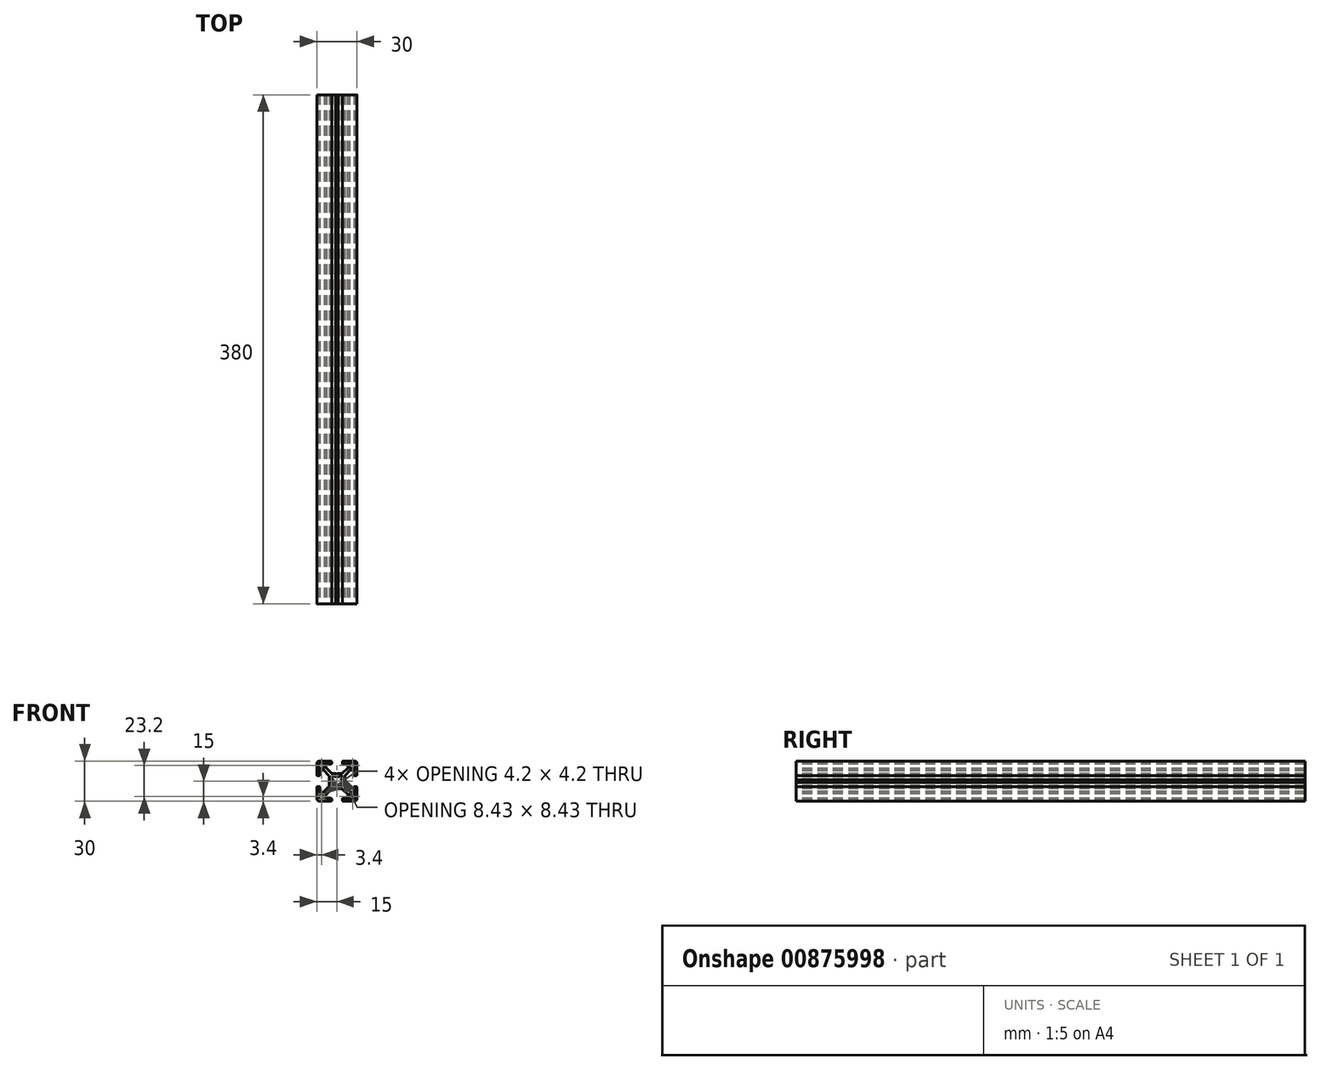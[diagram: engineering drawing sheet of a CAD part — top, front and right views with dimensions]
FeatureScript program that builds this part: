
annotation { "Feature Type Name" : "Feature", "Feature Type Description" : "" }
export const myFeature = defineFeature(function(context is Context, id is Id, definition is map)
    precondition{}
    {
        {
            var Q0;
            Q0=qCreatedBy(makeId("Front.planeOp"),FACE);
            var sketch = newSketch(context, id + "F0", { "sketchPlane" : qUnion([Q0])});
            skArc(sketch, "E0", {"start": v(9.88, 13.7) * mm, "mid": v(9.61, 13.59) * mm, "end": v(9.5, 13.32) * mm});
            skLineSegment(sketch, "E1", {"start": v(12.7, 13.7) * mm, "end": v(9.88, 13.7) * mm});
            skArc(sketch, "E2", {"start": v(13.7, 12.7) * mm, "mid": v(13.4, 13.4) * mm, "end": v(12.7, 13.7) * mm});
            skLineSegment(sketch, "E3", {"start": v(13.7, 9.88) * mm, "end": v(13.7, 12.7) * mm});
            skArc(sketch, "E4", {"start": v(13.32, 9.5) * mm, "mid": v(13.59, 9.61) * mm, "end": v(13.7, 9.88) * mm});
            skLineSegment(sketch, "E5", {"start": v(9.88, 9.5) * mm, "end": v(13.32, 9.5) * mm});
            skArc(sketch, "E6", {"start": v(9.5, 9.88) * mm, "mid": v(9.61, 9.61) * mm, "end": v(9.88, 9.5) * mm});
            skLineSegment(sketch, "E7", {"start": v(9.5, 13.32) * mm, "end": v(9.5, 9.88) * mm});
            skArc(sketch, "E8", {"start": v(-9.5, 13.32) * mm, "mid": v(-9.61, 13.59) * mm, "end": v(-9.88, 13.7) * mm});
            skLineSegment(sketch, "E9", {"start": v(-9.5, 9.88) * mm, "end": v(-9.5, 13.32) * mm});
            skArc(sketch, "E10", {"start": v(-9.88, 9.5) * mm, "mid": v(-9.61, 9.61) * mm, "end": v(-9.5, 9.88) * mm});
            skLineSegment(sketch, "E11", {"start": v(-13.32, 9.5) * mm, "end": v(-9.88, 9.5) * mm});
            skArc(sketch, "E12", {"start": v(-13.7, 9.88) * mm, "mid": v(-13.59, 9.61) * mm, "end": v(-13.32, 9.5) * mm});
            skLineSegment(sketch, "E13", {"start": v(-13.7, 12.7) * mm, "end": v(-13.7, 9.88) * mm});
            skArc(sketch, "E14", {"start": v(-12.7, 13.7) * mm, "mid": v(-13.4, 13.4) * mm, "end": v(-13.7, 12.7) * mm});
            skLineSegment(sketch, "E15", {"start": v(-9.88, 13.7) * mm, "end": v(-12.7, 13.7) * mm});
            skArc(sketch, "E16", {"start": v(-1.5, -3.2) * mm, "mid": v(0, -3.53) * mm, "end": v(1.5, -3.2) * mm});
            skLineSegment(sketch, "E17", {"start": v(-2.47, -3.98) * mm, "end": v(-1.5, -3.2) * mm});
            skArc(sketch, "E18", {"start": v(-3.98, -2.47) * mm, "mid": v(-3.9, -3.9) * mm, "end": v(-2.47, -3.98) * mm});
            skLineSegment(sketch, "E19", {"start": v(-3.2, -1.5) * mm, "end": v(-3.98, -2.47) * mm});
            skArc(sketch, "E20", {"start": v(-3.2, 1.5) * mm, "mid": v(-3.53, 0) * mm, "end": v(-3.2, -1.5) * mm});
            skLineSegment(sketch, "E21", {"start": v(-3.98, 2.47) * mm, "end": v(-3.2, 1.5) * mm});
            skArc(sketch, "E22", {"start": v(-2.47, 3.98) * mm, "mid": v(-3.9, 3.9) * mm, "end": v(-3.98, 2.47) * mm});
            skLineSegment(sketch, "E23", {"start": v(-1.5, 3.2) * mm, "end": v(-2.47, 3.98) * mm});
            skArc(sketch, "E24", {"start": v(1.5, 3.2) * mm, "mid": v(0, 3.53) * mm, "end": v(-1.5, 3.2) * mm});
            skLineSegment(sketch, "E25", {"start": v(2.47, 3.98) * mm, "end": v(1.5, 3.2) * mm});
            skArc(sketch, "E26", {"start": v(3.98, 2.47) * mm, "mid": v(3.9, 3.9) * mm, "end": v(2.47, 3.98) * mm});
            skLineSegment(sketch, "E27", {"start": v(3.2, 1.5) * mm, "end": v(3.98, 2.47) * mm});
            skArc(sketch, "E28", {"start": v(3.2, -1.5) * mm, "mid": v(3.53, 0) * mm, "end": v(3.2, 1.5) * mm});
            skLineSegment(sketch, "E29", {"start": v(3.98, -2.47) * mm, "end": v(3.2, -1.5) * mm});
            skArc(sketch, "E30", {"start": v(2.47, -3.98) * mm, "mid": v(3.9, -3.9) * mm, "end": v(3.98, -2.47) * mm});
            skLineSegment(sketch, "E31", {"start": v(1.5, -3.2) * mm, "end": v(2.47, -3.98) * mm});
            skArc(sketch, "E32", {"start": v(-13.32, -9.5) * mm, "mid": v(-13.59, -9.61) * mm, "end": v(-13.7, -9.88) * mm});
            skLineSegment(sketch, "E33", {"start": v(-9.88, -9.5) * mm, "end": v(-13.32, -9.5) * mm});
            skArc(sketch, "E34", {"start": v(-9.5, -9.88) * mm, "mid": v(-9.61, -9.61) * mm, "end": v(-9.88, -9.5) * mm});
            skLineSegment(sketch, "E35", {"start": v(-9.5, -13.32) * mm, "end": v(-9.5, -9.88) * mm});
            skArc(sketch, "E36", {"start": v(-9.88, -13.7) * mm, "mid": v(-9.61, -13.59) * mm, "end": v(-9.5, -13.32) * mm});
            skLineSegment(sketch, "E37", {"start": v(-12.7, -13.7) * mm, "end": v(-9.88, -13.7) * mm});
            skArc(sketch, "E38", {"start": v(-13.7, -12.7) * mm, "mid": v(-13.4, -13.4) * mm, "end": v(-12.7, -13.7) * mm});
            skLineSegment(sketch, "E39", {"start": v(-13.7, -9.88) * mm, "end": v(-13.7, -12.7) * mm});
            skArc(sketch, "E40", {"start": v(9.5, -13.32) * mm, "mid": v(9.61, -13.59) * mm, "end": v(9.88, -13.7) * mm});
            skLineSegment(sketch, "E41", {"start": v(9.5, -9.88) * mm, "end": v(9.5, -13.32) * mm});
            skArc(sketch, "E42", {"start": v(9.88, -9.5) * mm, "mid": v(9.61, -9.61) * mm, "end": v(9.5, -9.88) * mm});
            skLineSegment(sketch, "E43", {"start": v(13.32, -9.5) * mm, "end": v(9.88, -9.5) * mm});
            skArc(sketch, "E44", {"start": v(13.7, -9.88) * mm, "mid": v(13.59, -9.61) * mm, "end": v(13.32, -9.5) * mm});
            skLineSegment(sketch, "E45", {"start": v(13.7, -12.7) * mm, "end": v(13.7, -9.88) * mm});
            skArc(sketch, "E46", {"start": v(12.7, -13.7) * mm, "mid": v(13.4, -13.4) * mm, "end": v(13.7, -12.7) * mm});
            skLineSegment(sketch, "E47", {"start": v(9.88, -13.7) * mm, "end": v(12.7, -13.7) * mm});
            skArc(sketch, "E48", {"start": v(13.24, -4) * mm, "mid": v(12.89, -4.15) * mm, "end": v(12.74, -4.5) * mm});
            skLineSegment(sketch, "E49", {"start": v(12.74, -4.5) * mm, "end": v(12.74, -7.73) * mm});
            skArc(sketch, "E50", {"start": v(12.24, -8.25) * mm, "mid": v(12.6, -8.1) * mm, "end": v(12.74, -7.73) * mm});
            skLineSegment(sketch, "E51", {"start": v(12.24, -8.25) * mm, "end": v(10.26, -8.25) * mm});
            skArc(sketch, "E52", {"start": v(9.9, -8.1) * mm, "mid": v(10.07, -8.21) * mm, "end": v(10.26, -8.25) * mm});
            skLineSegment(sketch, "E53", {"start": v(9.9, -8.1) * mm, "end": v(5.98, -4.18) * mm});
            skArc(sketch, "E54", {"start": v(5.83, -3.82) * mm, "mid": v(5.87, -4.02) * mm, "end": v(5.98, -4.18) * mm});
            skLineSegment(sketch, "E55", {"start": v(5.83, -3.82) * mm, "end": v(5.83, -1.01) * mm});
            skLineSegment(sketch, "E56", {"start": v(5.83, -1.01) * mm, "end": v(5.32, -0.06) * mm});
            skLineSegment(sketch, "E57", {"start": v(5.32, -0.06) * mm, "end": v(5.83, 0.89) * mm});
            skLineSegment(sketch, "E58", {"start": v(5.83, 0.89) * mm, "end": v(5.83, 3.82) * mm});
            skArc(sketch, "E59", {"start": v(5.98, 4.18) * mm, "mid": v(5.87, 4.02) * mm, "end": v(5.83, 3.82) * mm});
            skLineSegment(sketch, "E60", {"start": v(5.98, 4.18) * mm, "end": v(9.9, 8.1) * mm});
            skArc(sketch, "E61", {"start": v(10.26, 8.25) * mm, "mid": v(10.07, 8.21) * mm, "end": v(9.9, 8.1) * mm});
            skLineSegment(sketch, "E62", {"start": v(10.26, 8.25) * mm, "end": v(12.24, 8.25) * mm});
            skArc(sketch, "E63", {"start": v(12.74, 7.73) * mm, "mid": v(12.6, 8.1) * mm, "end": v(12.24, 8.25) * mm});
            skLineSegment(sketch, "E64", {"start": v(12.74, 7.73) * mm, "end": v(12.74, 4.5) * mm});
            skArc(sketch, "E65", {"start": v(12.74, 4.5) * mm, "mid": v(12.89, 4.15) * mm, "end": v(13.24, 4) * mm});
            skLineSegment(sketch, "E66", {"start": v(13.24, 4) * mm, "end": v(14.5, 4) * mm});
            skArc(sketch, "E67", {"start": v(14.5, 4) * mm, "mid": v(14.85, 4.15) * mm, "end": v(15, 4.5) * mm});
            skLineSegment(sketch, "E68", {"start": v(15, 4.5) * mm, "end": v(15, 13) * mm});
            skArc(sketch, "E69", {"start": v(15, 13) * mm, "mid": v(14.41, 14.41) * mm, "end": v(13, 15) * mm});
            skLineSegment(sketch, "E70", {"start": v(13, 15) * mm, "end": v(4.5, 15) * mm});
            skArc(sketch, "E71", {"start": v(4.5, 15) * mm, "mid": v(4.15, 14.85) * mm, "end": v(4, 14.5) * mm});
            skLineSegment(sketch, "E72", {"start": v(4, 14.5) * mm, "end": v(4, 13.24) * mm});
            skArc(sketch, "E73", {"start": v(4, 13.24) * mm, "mid": v(4.15, 12.89) * mm, "end": v(4.5, 12.74) * mm});
            skLineSegment(sketch, "E74", {"start": v(4.5, 12.74) * mm, "end": v(7.73, 12.74) * mm});
            skArc(sketch, "E75", {"start": v(8.25, 12.24) * mm, "mid": v(8.1, 12.6) * mm, "end": v(7.73, 12.74) * mm});
            skLineSegment(sketch, "E76", {"start": v(8.25, 12.24) * mm, "end": v(8.25, 10.26) * mm});
            skArc(sketch, "E77", {"start": v(8.1, 9.9) * mm, "mid": v(8.21, 10.07) * mm, "end": v(8.25, 10.26) * mm});
            skLineSegment(sketch, "E78", {"start": v(8.1, 9.9) * mm, "end": v(4.18, 5.98) * mm});
            skArc(sketch, "E79", {"start": v(3.82, 5.83) * mm, "mid": v(4.02, 5.87) * mm, "end": v(4.18, 5.98) * mm});
            skLineSegment(sketch, "E80", {"start": v(3.82, 5.83) * mm, "end": v(0.95, 5.83) * mm});
            skLineSegment(sketch, "E81", {"start": v(0.95, 5.83) * mm, "end": v(0, 5.32) * mm});
            skLineSegment(sketch, "E82", {"start": v(0, 5.32) * mm, "end": v(-0.95, 5.83) * mm});
            skLineSegment(sketch, "E83", {"start": v(-0.95, 5.83) * mm, "end": v(-3.82, 5.83) * mm});
            skArc(sketch, "E84", {"start": v(-4.18, 5.98) * mm, "mid": v(-4.02, 5.87) * mm, "end": v(-3.82, 5.83) * mm});
            skLineSegment(sketch, "E85", {"start": v(-4.18, 5.98) * mm, "end": v(-8.1, 9.9) * mm});
            skArc(sketch, "E86", {"start": v(-8.25, 10.26) * mm, "mid": v(-8.21, 10.07) * mm, "end": v(-8.1, 9.9) * mm});
            skLineSegment(sketch, "E87", {"start": v(-8.25, 10.26) * mm, "end": v(-8.25, 12.24) * mm});
            skArc(sketch, "E88", {"start": v(-7.73, 12.74) * mm, "mid": v(-8.1, 12.6) * mm, "end": v(-8.25, 12.24) * mm});
            skLineSegment(sketch, "E89", {"start": v(-7.73, 12.74) * mm, "end": v(-4.5, 12.74) * mm});
            skArc(sketch, "E90", {"start": v(-4.5, 12.74) * mm, "mid": v(-4.15, 12.89) * mm, "end": v(-4, 13.24) * mm});
            skLineSegment(sketch, "E91", {"start": v(-4, 13.24) * mm, "end": v(-4, 14.5) * mm});
            skArc(sketch, "E92", {"start": v(-4, 14.5) * mm, "mid": v(-4.15, 14.85) * mm, "end": v(-4.5, 15) * mm});
            skLineSegment(sketch, "E93", {"start": v(-4.5, 15) * mm, "end": v(-13, 15) * mm});
            skArc(sketch, "E94", {"start": v(-13, 15) * mm, "mid": v(-14.41, 14.41) * mm, "end": v(-15, 13) * mm});
            skLineSegment(sketch, "E95", {"start": v(-15, 13) * mm, "end": v(-15, 4.5) * mm});
            skArc(sketch, "E96", {"start": v(-15, 4.5) * mm, "mid": v(-14.85, 4.15) * mm, "end": v(-14.5, 4) * mm});
            skLineSegment(sketch, "E97", {"start": v(-14.5, 4) * mm, "end": v(-13.24, 4) * mm});
            skArc(sketch, "E98", {"start": v(-13.24, 4) * mm, "mid": v(-12.89, 4.15) * mm, "end": v(-12.74, 4.5) * mm});
            skLineSegment(sketch, "E99", {"start": v(-12.74, 4.5) * mm, "end": v(-12.74, 7.73) * mm});
            skArc(sketch, "E100", {"start": v(-12.24, 8.25) * mm, "mid": v(-12.6, 8.1) * mm, "end": v(-12.74, 7.73) * mm});
            skLineSegment(sketch, "E101", {"start": v(-12.24, 8.25) * mm, "end": v(-10.26, 8.25) * mm});
            skArc(sketch, "E102", {"start": v(-9.9, 8.1) * mm, "mid": v(-10.07, 8.21) * mm, "end": v(-10.26, 8.25) * mm});
            skLineSegment(sketch, "E103", {"start": v(-9.9, 8.1) * mm, "end": v(-5.98, 4.18) * mm});
            skArc(sketch, "E104", {"start": v(-5.83, 3.82) * mm, "mid": v(-5.87, 4.02) * mm, "end": v(-5.98, 4.18) * mm});
            skLineSegment(sketch, "E105", {"start": v(-5.83, 3.82) * mm, "end": v(-5.83, 0.89) * mm});
            skLineSegment(sketch, "E106", {"start": v(-5.83, 0.89) * mm, "end": v(-5.32, -0.06) * mm});
            skLineSegment(sketch, "E107", {"start": v(-5.32, -0.06) * mm, "end": v(-5.83, -1.01) * mm});
            skLineSegment(sketch, "E108", {"start": v(-5.83, -1.01) * mm, "end": v(-5.83, -3.82) * mm});
            skArc(sketch, "E109", {"start": v(-5.98, -4.18) * mm, "mid": v(-5.87, -4.02) * mm, "end": v(-5.83, -3.82) * mm});
            skLineSegment(sketch, "E110", {"start": v(-5.98, -4.18) * mm, "end": v(-9.9, -8.1) * mm});
            skArc(sketch, "E111", {"start": v(-10.26, -8.25) * mm, "mid": v(-10.07, -8.21) * mm, "end": v(-9.9, -8.1) * mm});
            skLineSegment(sketch, "E112", {"start": v(-10.26, -8.25) * mm, "end": v(-12.24, -8.25) * mm});
            skArc(sketch, "E113", {"start": v(-12.74, -7.73) * mm, "mid": v(-12.6, -8.1) * mm, "end": v(-12.24, -8.25) * mm});
            skLineSegment(sketch, "E114", {"start": v(-12.74, -7.73) * mm, "end": v(-12.74, -4.5) * mm});
            skArc(sketch, "E115", {"start": v(-12.74, -4.5) * mm, "mid": v(-12.89, -4.15) * mm, "end": v(-13.24, -4) * mm});
            skLineSegment(sketch, "E116", {"start": v(-13.24, -4) * mm, "end": v(-14.5, -4) * mm});
            skArc(sketch, "E117", {"start": v(-14.5, -4) * mm, "mid": v(-14.85, -4.15) * mm, "end": v(-15, -4.5) * mm});
            skLineSegment(sketch, "E118", {"start": v(-15, -4.5) * mm, "end": v(-15, -13) * mm});
            skArc(sketch, "E119", {"start": v(-15, -13) * mm, "mid": v(-14.41, -14.41) * mm, "end": v(-13, -15) * mm});
            skLineSegment(sketch, "E120", {"start": v(-13, -15) * mm, "end": v(-4.5, -15) * mm});
            skArc(sketch, "E121", {"start": v(-4.5, -15) * mm, "mid": v(-4.15, -14.85) * mm, "end": v(-4, -14.5) * mm});
            skLineSegment(sketch, "E122", {"start": v(-4, -14.5) * mm, "end": v(-4, -13.24) * mm});
            skArc(sketch, "E123", {"start": v(-4, -13.24) * mm, "mid": v(-4.15, -12.89) * mm, "end": v(-4.5, -12.74) * mm});
            skLineSegment(sketch, "E124", {"start": v(-4.5, -12.74) * mm, "end": v(-7.73, -12.74) * mm});
            skArc(sketch, "E125", {"start": v(-8.25, -12.24) * mm, "mid": v(-8.1, -12.6) * mm, "end": v(-7.73, -12.74) * mm});
            skLineSegment(sketch, "E126", {"start": v(-8.25, -12.24) * mm, "end": v(-8.25, -10.26) * mm});
            skArc(sketch, "E127", {"start": v(-8.1, -9.9) * mm, "mid": v(-8.21, -10.07) * mm, "end": v(-8.25, -10.26) * mm});
            skLineSegment(sketch, "E128", {"start": v(-8.1, -9.9) * mm, "end": v(-4.18, -5.98) * mm});
            skArc(sketch, "E129", {"start": v(-3.82, -5.83) * mm, "mid": v(-4.02, -5.87) * mm, "end": v(-4.18, -5.98) * mm});
            skLineSegment(sketch, "E130", {"start": v(-3.82, -5.83) * mm, "end": v(-0.95, -5.83) * mm});
            skLineSegment(sketch, "E131", {"start": v(-0.95, -5.83) * mm, "end": v(0, -5.32) * mm});
            skLineSegment(sketch, "E132", {"start": v(0, -5.32) * mm, "end": v(0.95, -5.83) * mm});
            skLineSegment(sketch, "E133", {"start": v(0.95, -5.83) * mm, "end": v(3.82, -5.83) * mm});
            skArc(sketch, "E134", {"start": v(4.18, -5.98) * mm, "mid": v(4.02, -5.87) * mm, "end": v(3.82, -5.83) * mm});
            skLineSegment(sketch, "E135", {"start": v(4.18, -5.98) * mm, "end": v(8.1, -9.9) * mm});
            skArc(sketch, "E136", {"start": v(8.25, -10.26) * mm, "mid": v(8.21, -10.07) * mm, "end": v(8.1, -9.9) * mm});
            skLineSegment(sketch, "E137", {"start": v(8.25, -10.26) * mm, "end": v(8.25, -12.24) * mm});
            skArc(sketch, "E138", {"start": v(7.73, -12.74) * mm, "mid": v(8.1, -12.6) * mm, "end": v(8.25, -12.24) * mm});
            skLineSegment(sketch, "E139", {"start": v(7.73, -12.74) * mm, "end": v(4.5, -12.74) * mm});
            skArc(sketch, "E140", {"start": v(4.5, -12.74) * mm, "mid": v(4.15, -12.89) * mm, "end": v(4, -13.24) * mm});
            skLineSegment(sketch, "E141", {"start": v(4, -13.24) * mm, "end": v(4, -14.5) * mm});
            skArc(sketch, "E142", {"start": v(4, -14.5) * mm, "mid": v(4.15, -14.85) * mm, "end": v(4.5, -15) * mm});
            skLineSegment(sketch, "E143", {"start": v(4.5, -15) * mm, "end": v(13, -15) * mm});
            skArc(sketch, "E144", {"start": v(13, -15) * mm, "mid": v(14.41, -14.41) * mm, "end": v(15, -13) * mm});
            skLineSegment(sketch, "E145", {"start": v(15, -13) * mm, "end": v(15, -4.5) * mm});
            skArc(sketch, "E146", {"start": v(15, -4.5) * mm, "mid": v(14.85, -4.15) * mm, "end": v(14.5, -4) * mm});
            skLineSegment(sketch, "E147", {"start": v(14.5, -4) * mm, "end": v(13.24, -4) * mm});
            skSolve(sketch);
        }
        {
            var Q0;
            Q0=qCreatedBy(makeId("Top.planeOp"),FACE);
            var sketch = newSketch(context, id + "F1", { "sketchPlane" : qUnion([Q0])});
            skLineSegment(sketch, "E148", {"start": v(-1.5, 190) * mm, "end": v(-1.5, -190) * mm});
            skSolve(sketch);
        }
        {
            var Q0;
            Q0=qSketchRegion(id+"F0",true);
            var Q1;
            Q1=sQuery(id+"F1.wireOp",EDGE,"E148");
            var Q2;
            Q2=sQuery(id+"F1.wireOp",EDGE,"fSjTIPXa-SZZ6-Uh3d-dTjF-iSAX6K3vTkU0");
            var Q3;
            Q3=sQuery(id+"F1.wireOp",EDGE,"X1iaMUp9-18Uv-Qplb-D4Eo-NhRo6oMLb04g");
            var Q4;
            Q4=sQuery(id+"F1.wireOp",EDGE,"ysMRVMGi-oqtn-a0SZ-pmm6-otZbrj3hBrry");
            sweep(context, id + "F2", {"profiles" : qUnion([Q0]), "path" : qUnion([Q1, Q2, Q3, Q4])});
        }
    });
